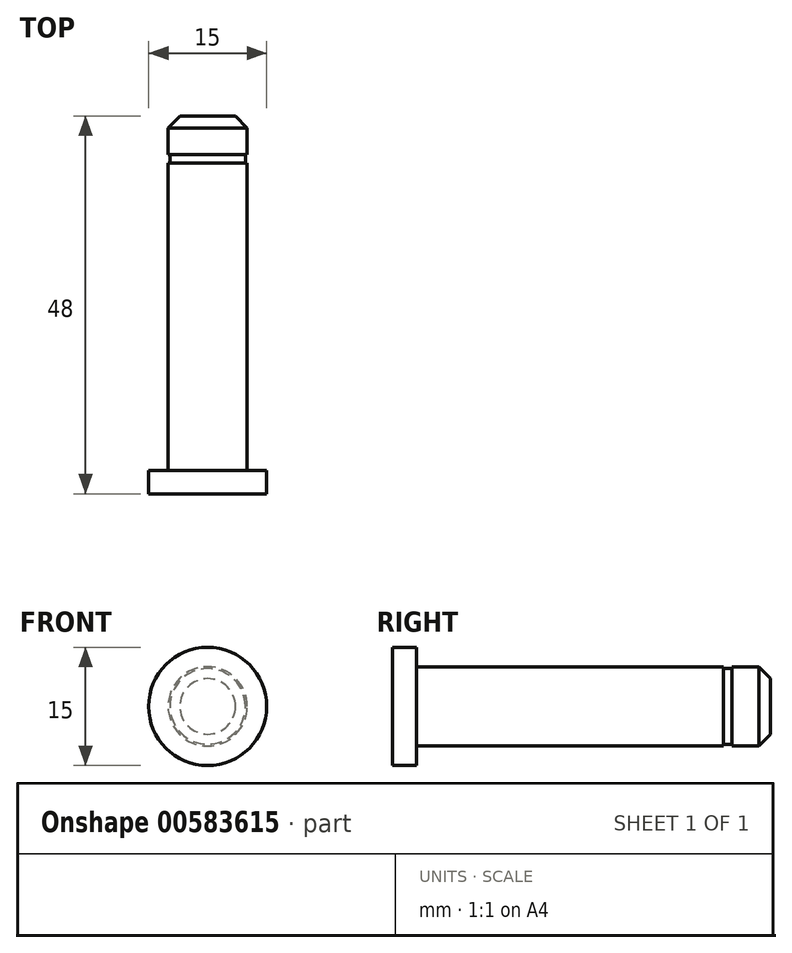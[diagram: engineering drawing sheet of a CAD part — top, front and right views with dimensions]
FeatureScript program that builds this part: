
annotation { "Feature Type Name" : "Feature", "Feature Type Description" : "" }
export const myFeature = defineFeature(function(context is Context, id is Id, definition is map)
    precondition{}
    {
        {
            var Q0;
            Q0=qCreatedBy(makeId("Right.planeOp"),FACE);
            var sketch = newSketch(context, id + "F0", { "sketchPlane" : qUnion([Q0])});
            skLineSegment(sketch, "E0.top", {"start": v(-21, 7.5) * mm, "end": v(-24, 7.5) * mm});
            skLineSegment(sketch, "E0.left", {"start": v(24, 0) * mm, "end": v(24, 5.03) * mm});
            skLineSegment(sketch, "E0.right", {"start": v(-24, 0) * mm, "end": v(-24, 7.5) * mm});
            skPoint(sketch, "E0.middle", {"position": v(0, 0) * mm});
            skLineSegment(sketch, "E1", {"start": v(-21, 7.5) * mm, "end": v(-21, 5.03) * mm});
            skLineSegment(sketch, "E2.top", {"start": v(24, 5.03) * mm, "end": v(19.1, 5.03) * mm});
            skLineSegment(sketch, "E3.top", {"start": v(19.1, 4.8) * mm, "end": v(18, 4.8) * mm});
            skLineSegment(sketch, "E4", {"start": v(18, 5.03) * mm, "end": v(18, 4.8) * mm});
            skLineSegment(sketch, "E5", {"start": v(19.1, 5.03) * mm, "end": v(19.1, 4.8) * mm});
            skLineSegment(sketch, "E6.trimOffspring", {"start": v(18, 5.03) * mm, "end": v(-21, 5.03) * mm});
            skLineSegment(sketch, "E7", {"start": v(-24, 0) * mm, "end": v(24, 0) * mm});
            skSolve(sketch);
        }
        {
            var Q0;
            Q0=makeQuery(id+"F0.imprint","IMPRINT",FACE,{"disambiguationData":[TD([[makeQuery(id+"F0.imprint","IMPRINT",EDGE,{"derivedFrom":sQuery(id+"F0.wireOp",EDGE,"E0.top")}),1.0]])]});
            var Q1;
            Q1=sQuery(id+"F0.wireOp",EDGE,"E7");
            revolve(context, id + "F1", {"entities" : qUnion([Q0]), "axis" : qUnion([Q1]), "revolveType" : RevolveType.FULL});
        }
        {
            var Q0;
            Q0=makeQuery(id+"F1.opRevolve","SWEPT_EDGE",EDGE,{"disambiguationData":[OSD([sQuery(id+"F0.wireOp",EDGE,"E2.top"),sQuery(id+"F0.wireOp",EDGE,"E0.left")])]});
            chamfer(context, id + "F2", {"entities" : qUnion([Q0]), "width" : 1.5 * mm, "tangentPropagation" : true});
        }
    });
